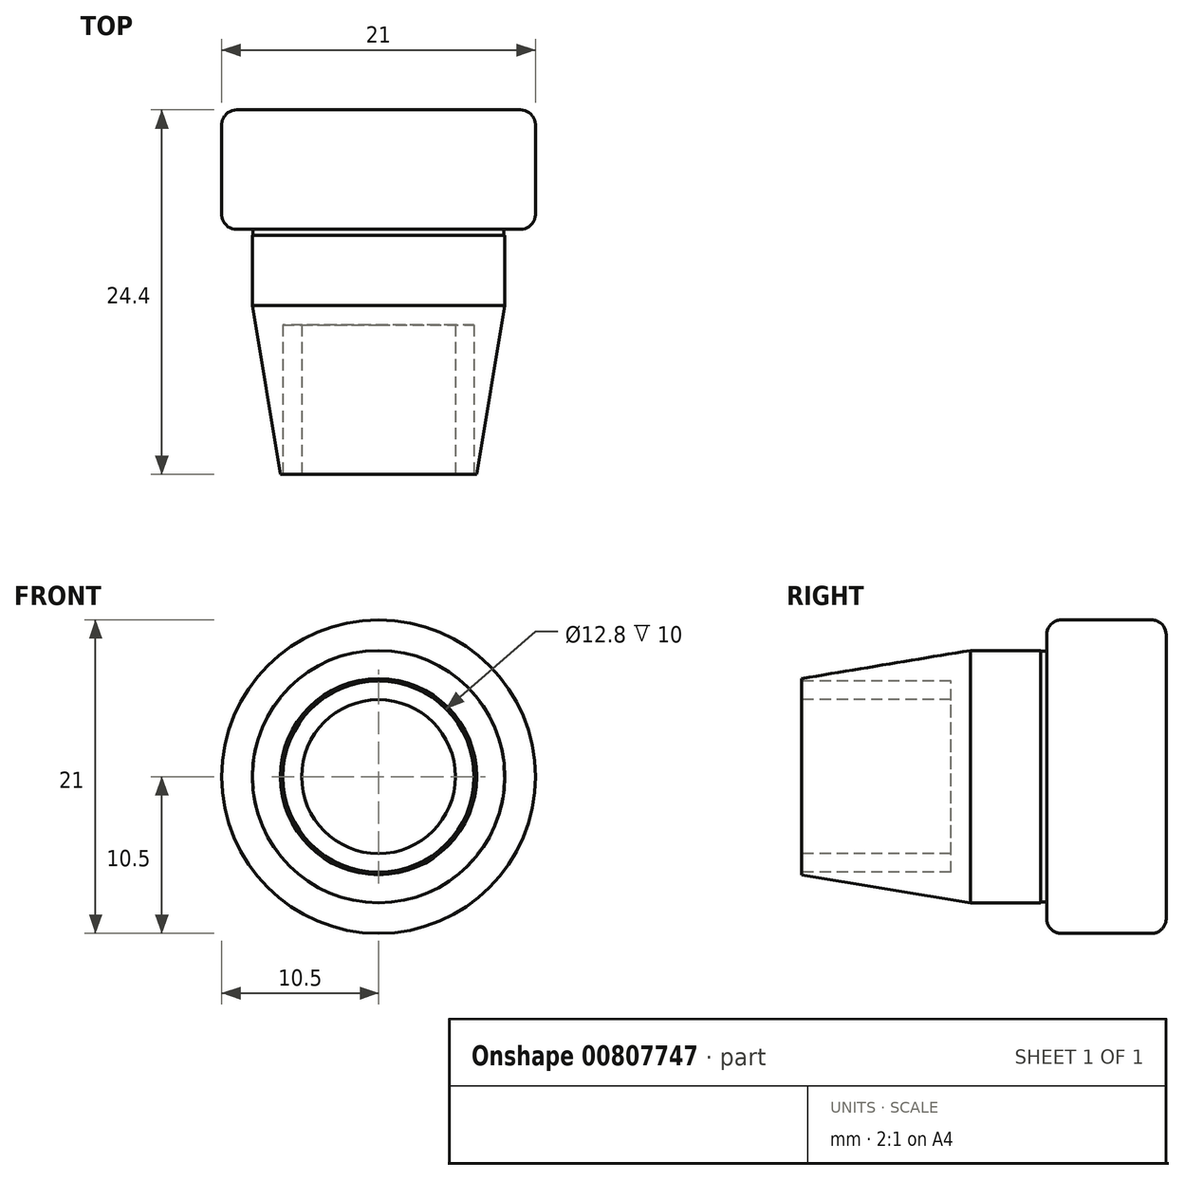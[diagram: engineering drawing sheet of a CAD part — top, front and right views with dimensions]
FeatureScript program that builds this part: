
annotation { "Feature Type Name" : "Feature", "Feature Type Description" : "" }
export const myFeature = defineFeature(function(context is Context, id is Id, definition is map)
    precondition{}
    {
        {
            var Q0;
            Q0=qCreatedBy(makeId("Front.planeOp"),FACE);
            var sketch = newSketch(context, id + "F0", { "sketchPlane" : qUnion([Q0])});
            skCircle(sketch, "E0", {"center": v(0, 0) * mm, "radius": 10.5 * mm});
            skSolve(sketch);
        }
        {
            var Q0;
            Q0=makeQuery(id+"F0.imprint","IMPRINT",FACE,{"disambiguationData":[TD([[makeQuery(id+"F0.imprint","IMPRINT",EDGE,{"derivedFrom":sQuery(id+"F0.wireOp",EDGE,"E0")}),1.0]])]});
            extrude(context, id + "F1", {"entities" : qUnion([Q0]), "depth" : 8 * mm, "offsetDistance" : 25 * mm});
        }
        {
            var Q0;
            Q0=makeQuery(id+"F1.opExtrude","CAP_FACE",FACE,{"disambiguationData":[OSD([sQuery(id+"F0.wireOp",EDGE,"E0")])],"isStart":false});
            var sketch = newSketch(context, id + "F2", { "sketchPlane" : qUnion([Q0])});
            skCircle(sketch, "E1", {"center": v(0, 0) * mm, "radius": 8.4 * mm});
            skSolve(sketch);
        }
        {
            var Q0;
            Q0=makeQuery(id+"F2.imprint","IMPRINT",FACE,{"disambiguationData":[TD([[makeQuery(id+"F2.imprint","IMPRINT",EDGE,{"derivedFrom":sQuery(id+"F2.wireOp",EDGE,"E1")}),1.0]])]});
            extrude(context, id + "F3", {"entities" : qUnion([Q0]), "operationType" : NewBodyOperationType.ADD, "depth" : .4 * mm, "offsetDistance" : 25 * mm});
        }
        {
            var Q0;
            Q0=makeQuery(id+"F3.opExtrude","CAP_FACE",FACE,{"disambiguationData":[OSD([sQuery(id+"F2.wireOp",EDGE,"E1")])],"isStart":false});
            var sketch = newSketch(context, id + "F4", { "sketchPlane" : qUnion([Q0])});
            skCircle(sketch, "E2", {"center": v(0, 0) * mm, "radius": 8.45 * mm});
            skSolve(sketch);
        }
        {
            var Q0;
            Q0=makeQuery(id+"F4.imprint","IMPRINT",FACE,{"disambiguationData":[TD([[makeQuery(id+"F4.imprint","IMPRINT",EDGE,{"derivedFrom":sQuery(id+"F4.wireOp",EDGE,"E2")}),1.0]])]});
            var Q1;
            Q1=makeQuery(id+"F4.imprint","IMPRINT",FACE,{"disambiguationData":[TD([[makeQuery(id+"F4.imprint","IMPRINT",EDGE,{"derivedFrom":makeQuery(id+"F3.opExtrude","CAP_EDGE",EDGE,{"disambiguationData":[OSD([sQuery(id+"F2.wireOp",EDGE,"E1")])],"isStart":false})}),1.0]])]});
            extrude(context, id + "F5", {"entities" : qUnion([Q0, Q1]), "operationType" : NewBodyOperationType.ADD, "depth" : 16 * mm, "offsetDistance" : 25 * mm});
        }
        {
            var Q0;
            Q0=makeQuery(id+"F5.opExtrude","CAP_FACE",FACE,{"disambiguationData":[OSD([sQuery(id+"F4.wireOp",EDGE,"E2")])],"isStart":false});
            var sketch = newSketch(context, id + "F6", { "sketchPlane" : qUnion([Q0])});
            skCircle(sketch, "E3", {"center": v(0, 0) * mm, "radius": 6.4 * mm});
            skCircle(sketch, "E4", {"center": v(0, 0) * mm, "radius": 5.15 * mm});
            skSolve(sketch);
        }
        {
            var Q0;
            Q0=makeQuery(id+"F6.imprint","IMPRINT",FACE,{"disambiguationData":[TD([[makeQuery(id+"F6.imprint","IMPRINT",EDGE,{"derivedFrom":sQuery(id+"F6.wireOp",EDGE,"E3")}),1.0]])]});
            extrude(context, id + "F7", {"entities" : qUnion([Q0]), "operationType" : NewBodyOperationType.REMOVE, "oppositeDirection" : true, "depth" : 10 * mm, "offsetDistance" : 25 * mm});
        }
        {
            var Q0;
            Q0=qCreatedBy(makeId("Right.planeOp"),FACE);
            var sketch = newSketch(context, id + "F8", { "sketchPlane" : qUnion([Q0])});
            skLineSegment(sketch, "E5", {"start": v(-24.4, 8.57) * mm, "end": v(-24.4, 6.57) * mm});
            skLineSegment(sketch, "E6", {"start": v(-24.4, 6.57) * mm, "end": v(-12.4, 8.57) * mm});
            skLineSegment(sketch, "E7", {"start": v(-12.4, 8.57) * mm, "end": v(-24.4, 8.57) * mm});
            skLineSegment(sketch, "E8", {"start": v(-12.4, 8.57) * mm, "end": v(-12.4, -8.42) * mm});
            skLineSegment(sketch, "E9", {"start": v(-12.4, 0) * mm, "end": v(-24.4, 0) * mm});
            skSolve(sketch);
        }
        {
            var Q0;
            Q0 = qSketchRegion(id + "F8", true);
            var Q1;
            Q1=sQuery(id+"F8.wireOp",EDGE,"E9");
            revolve(context, id + "F9", {"operationType" : NewBodyOperationType.REMOVE, "surfaceOperationType" : NewSurfaceOperationType.NEW, "entities" : qUnion([Q0]), "axis" : qUnion([Q1]), "revolveType" : RevolveType.FULL});
        }
        {
            var Q0;
            Q0=makeQuery(id+"F1.opExtrude","CAP_EDGE",EDGE,{"disambiguationData":[OSD([sQuery(id+"F0.wireOp",EDGE,"E0")])],"isStart":false});
            var Q1;
            Q1=makeQuery(id+"F1.opExtrude","CAP_EDGE",EDGE,{"disambiguationData":[OSD([sQuery(id+"F0.wireOp",EDGE,"E0")])],"isStart":true});
            fillet(context, id + "F10", {"entities" : qUnion([Q0, Q1]), "radius" : 1 * mm, "tangentPropagation" : true, "allowEdgeOverflow" : false});
        }
    });
